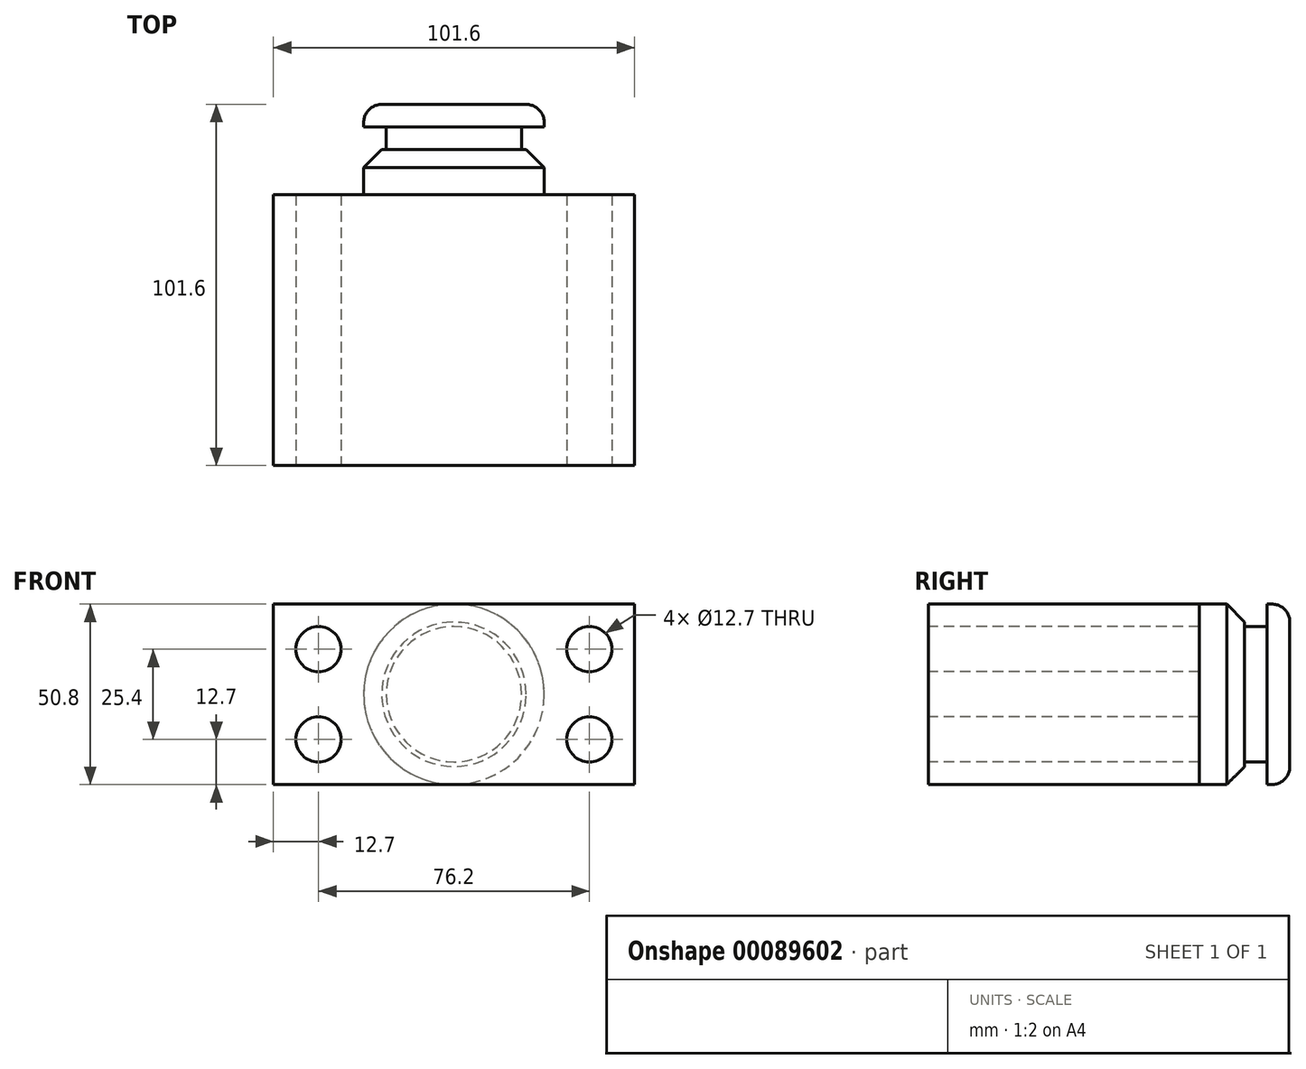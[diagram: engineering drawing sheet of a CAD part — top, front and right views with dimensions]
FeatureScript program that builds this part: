
annotation { "Feature Type Name" : "Feature", "Feature Type Description" : "" }
export const myFeature = defineFeature(function(context is Context, id is Id, definition is map)
    precondition{}
    {
        {
            var Q0;
            Q0=qCreatedBy(makeId("Front.planeOp"),FACE);
            var sketch = newSketch(context, id + "F0", { "sketchPlane" : qUnion([Q0])});
            skLineSegment(sketch, "E0", {"start": v(-50.8, 25.4) * mm, "end": v(50.8, 25.4) * mm});
            skLineSegment(sketch, "E1", {"start": v(50.8, 25.4) * mm, "end": v(50.8, -25.4) * mm});
            skLineSegment(sketch, "E2", {"start": v(50.8, -25.4) * mm, "end": v(-50.8, -25.4) * mm});
            skLineSegment(sketch, "E3", {"start": v(-50.8, 25.4) * mm, "end": v(-50.8, -25.4) * mm});
            skSolve(sketch);
        }
        {
            var Q0;
            Q0 = qSketchRegion(id + "F0", true);
            extrude(context, id + "F1", {"entities" : qUnion([Q0]), "depth" : 76.2 * mm});
        }
        {
            var Q0;
            Q0=makeQuery(id+"F1.opExtrude","CAP_FACE",FACE,{"disambiguationData":[OSD([sQuery(id+"F0.wireOp",EDGE,"E0"),sQuery(id+"F0.wireOp",EDGE,"E1"),sQuery(id+"F0.wireOp",EDGE,"E2"),sQuery(id+"F0.wireOp",EDGE,"E3")])],"isStart":false});
            var sketch = newSketch(context, id + "F2", { "sketchPlane" : qUnion([Q0])});
            skCircle(sketch, "E4", {"center": v(-38.1, 12.7) * mm, "radius": 6.35 * mm});
            skCircle(sketch, "E5", {"center": v(-38.1, -12.7) * mm, "radius": 6.35 * mm});
            skLineSegment(sketch, "E6", {"start": v(0, 46.1) * mm, "end": v(0, -34.32) * mm, "construction": true});
            skCircle(sketch, "E7.MirrorC", {"center": v(38.1, 12.7) * mm, "radius": 6.35 * mm});
            skCircle(sketch, "E8.MirrorC", {"center": v(38.1, -12.7) * mm, "radius": 6.35 * mm});
            skSolve(sketch);
        }
        {
            var Q0;
            Q0 = qSketchRegion(id + "F2", true);
            extrude(context, id + "F3", {"entities" : qUnion([Q0]), "operationType" : NewBodyOperationType.REMOVE, "endBound" : BoundingType.THROUGH_ALL, "oppositeDirection" : true, "depth" : 25.4 * mm});
        }
        {
            var Q0;
            Q0=qCreatedBy(makeId("Top.planeOp"),FACE);
            var sketch = newSketch(context, id + "F4", { "sketchPlane" : qUnion([Q0])});
            skLineSegment(sketch, "E9", {"start": v(0, 25.4) * mm, "end": v(-25.4, 25.4) * mm});
            skLineSegment(sketch, "E10", {"start": v(-25.4, 25.4) * mm, "end": v(-25.4, 0) * mm});
            skLineSegment(sketch, "E11", {"start": v(0, 25.4) * mm, "end": v(0, 0) * mm});
            skLineSegment(sketch, "E12", {"start": v(-25.4, 0) * mm, "end": v(0, 0) * mm});
            skSolve(sketch);
        }
        {
            var Q0;
            Q0=makeQuery(id+"F4.imprint","IMPRINT",FACE,{"disambiguationData":[TD([[makeQuery(id+"F4.imprint","IMPRINT",EDGE,{"derivedFrom":sQuery(id+"F4.wireOp",EDGE,"E9")}),1.0]])]});
            var Q1;
            Q1=sQuery(id+"F4.wireOp",EDGE,"E11");
            revolve(context, id + "F5", {"operationType" : NewBodyOperationType.ADD, "entities" : qUnion([Q0]), "axis" : qUnion([Q1]), "revolveType" : RevolveType.FULL});
        }
        {
            var Q0;
            Q0=qCreatedBy(makeId("Top.planeOp"),FACE);
            var sketch = newSketch(context, id + "F6", { "sketchPlane" : qUnion([Q0])});
            skLineSegment(sketch, "E13", {"start": v(0, 71.08) * mm, "end": v(0, -91.7) * mm, "construction": true});
            skLineSegment(sketch, "E14", {"start": v(-25.4, 12.7) * mm, "end": v(-25.4, 19.05) * mm});
            skLineSegment(sketch, "E15", {"start": v(-25.4, 19.05) * mm, "end": v(-19.05, 19.05) * mm});
            skLineSegment(sketch, "E16", {"start": v(-19.05, 19.05) * mm, "end": v(-19.05, 12.7) * mm});
            skLineSegment(sketch, "E17", {"start": v(-19.05, 12.7) * mm, "end": v(-25.4, 12.7) * mm});
            skSolve(sketch);
        }
        {
            var Q0;
            Q0 = qSketchRegion(id + "F6", true);
            var Q1;
            Q1=sQuery(id+"F6.wireOp",EDGE,"E13");
            revolve(context, id + "F7", {"operationType" : NewBodyOperationType.REMOVE, "entities" : qUnion([Q0]), "axis" : qUnion([Q1]), "revolveType" : RevolveType.FULL, "oppositeDirection" : true});
        }
        {
            var Q0;
            Q0=makeQuery(id+"F5.opRevolve","SWEPT_FACE",FACE,{"disambiguationData":[OSD([sQuery(id+"F4.wireOp",EDGE,"E9")])]});
            fillet(context, id + "F8", {"entities" : qUnion([Q0]), "radius" : 5.08 * mm, "tangentPropagation" : true, "allowEdgeOverflow" : false});
        }
        {
            var Q0;
            Q0=makeQuery(id+"F7.boolean.opBoolean","COPY",EDGE,{"derivedFrom":makeQuery(id+"F7.opRevolve","SWEPT_EDGE",EDGE,{"disambiguationData":[OSD([sQuery(id+"F6.wireOp",EDGE,"E14"),sQuery(id+"F6.wireOp",EDGE,"E17")])]})});
            chamfer(context, id + "F9", {"entities" : qUnion([Q0]), "width" : 5.08 * mm, "tangentPropagation" : true});
        }
    });
